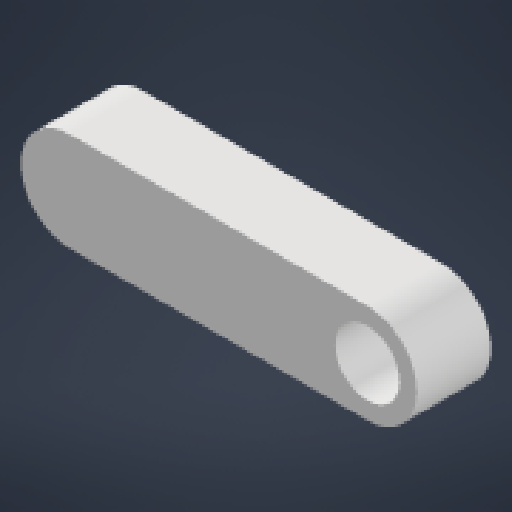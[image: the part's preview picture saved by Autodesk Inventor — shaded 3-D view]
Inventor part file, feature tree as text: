
AUTODESK INVENTOR PART (.ipt)
format: ipt  version: 2024.3 (Build 283343000, 343)  size: 135,168 bytes
history: native  units: in
note: dims shown in document units (in); Inventor stores cm internally (conversion verified against a paired STEP export)
features: extrude x1, fillet x1, sketch x1
ambient origin geometry x8: Origin, YZ Plane, XZ Plane, XY Plane, X Axis, Y Axis, Z Axis, Center Point
bodies: Solid1 (feature_tree)
feature tree (3):
  extrude  "Extrusion1"  Depth=0.75in
  fillet  "Fillet1"  Radius=0.375in
  sketch  "Sketch1"  dims[d0=0.163in d2=0.75in d3=0.375in d4=0.1875in d5=0.0in d6=0.0625in]
